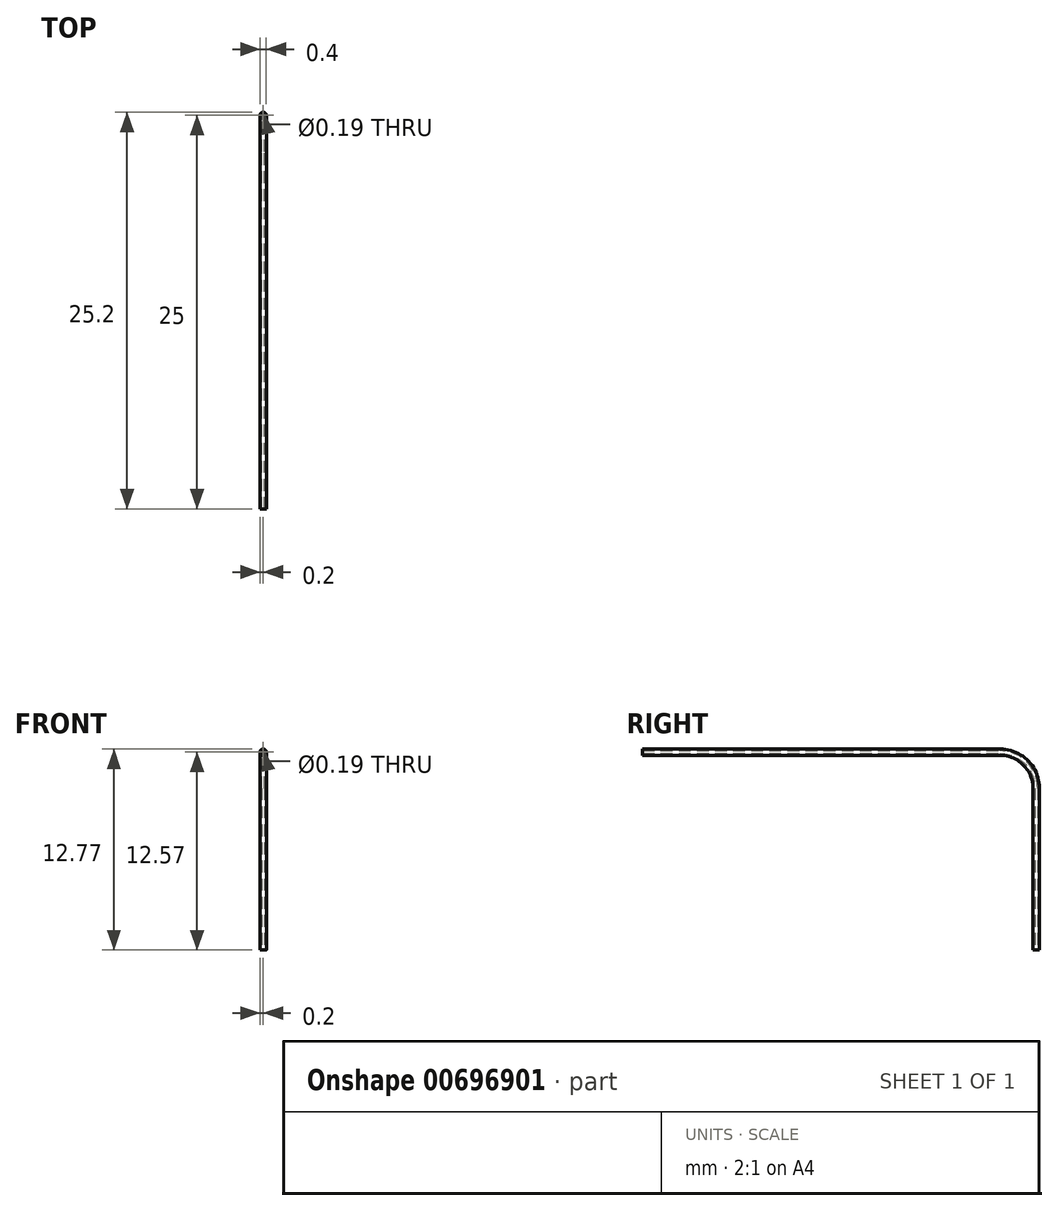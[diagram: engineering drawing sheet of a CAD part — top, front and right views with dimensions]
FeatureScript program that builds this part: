
annotation { "Feature Type Name" : "Feature", "Feature Type Description" : "" }
export const myFeature = defineFeature(function(context is Context, id is Id, definition is map)
    precondition{}
    {
        {
            var Q0;
            Q0=qCreatedBy(makeId("Right.planeOp"),FACE);
            var sketch = newSketch(context, id + "F0", { "sketchPlane" : qUnion([Q0])});
            skLineSegment(sketch, "E0", {"start": v(0, 0) * mm, "end": v(22.71, 0) * mm});
            skLineSegment(sketch, "E1", {"start": v(25, -2.29) * mm, "end": v(25, -12.57) * mm});
            skPoint(sketch, "E2.visualSharp", {"position": v(25, 0) * mm});
            skArc(sketch, "E2.filletArc", {"start": v(25, -2.29) * mm, "mid": v(24.33, -0.67) * mm, "end": v(22.71, 0) * mm});
            skSolve(sketch);
        }
        {
            var Q0;
            Q0=qCreatedBy(makeId("Front.planeOp"),FACE);
            var sketch = newSketch(context, id + "F1", { "sketchPlane" : qUnion([Q0])});
            skCircle(sketch, "E3", {"center": v(0, 0) * mm, "radius": 0.2 * mm});
            skCircle(sketch, "E4", {"center": v(0, 0) * mm, "radius": 0.1 * mm});
            skSolve(sketch);
        }
        {
            var Q0;
            Q0 = qSketchRegion(id + "F1", true);
            var Q1;
            Q1 = qConstructionFilter(qBodyType(qCreatedBy(id + "F0" ,EDGE), BodyType.WIRE), ConstructionObject.NO);
            sweep(context, id + "F2", {"profiles" : qUnion([Q0]), "path" : qUnion([Q1])});
        }
    });
